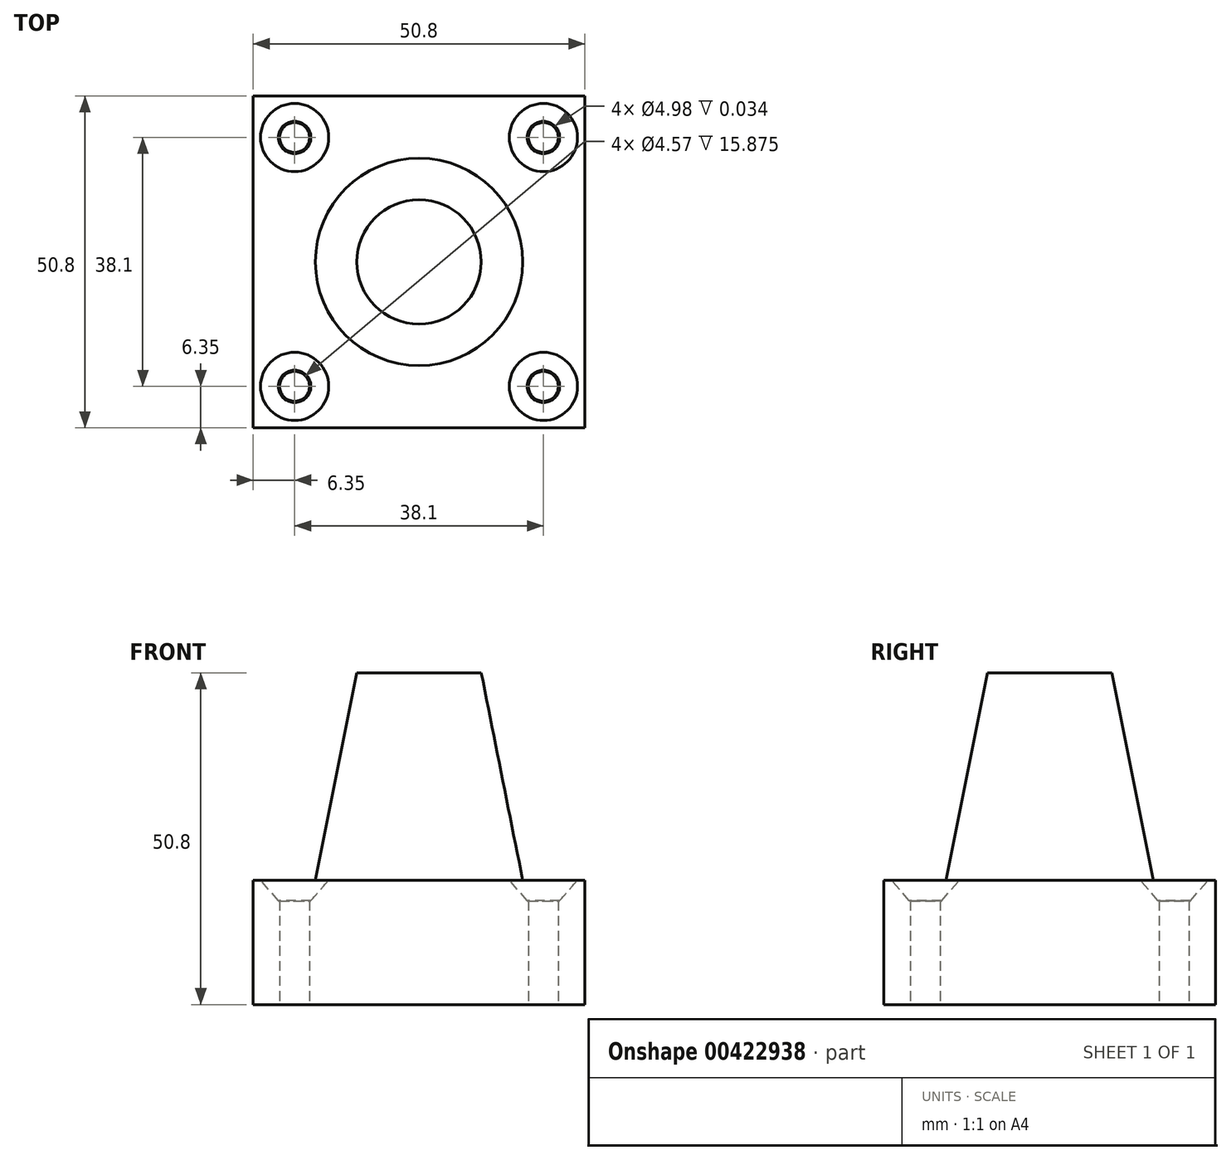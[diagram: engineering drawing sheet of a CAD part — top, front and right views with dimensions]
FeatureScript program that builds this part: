
annotation { "Feature Type Name" : "Feature", "Feature Type Description" : "" }
export const myFeature = defineFeature(function(context is Context, id is Id, definition is map)
    precondition{}
    {
        {
            var Q0;
            Q0=qCreatedBy(makeId("Top.planeOp"),FACE);
            var sketch = newSketch(context, id + "F0", { "sketchPlane" : qUnion([Q0])});
            skLineSegment(sketch, "E0.bottom", {"start": v(25.4, 25.4) * mm, "end": v(-25.4, 25.4) * mm});
            skLineSegment(sketch, "E0.top", {"start": v(25.4, -25.4) * mm, "end": v(-25.4, -25.4) * mm});
            skLineSegment(sketch, "E0.left", {"start": v(25.4, 25.4) * mm, "end": v(25.4, -25.4) * mm});
            skLineSegment(sketch, "E0.right", {"start": v(-25.4, 25.4) * mm, "end": v(-25.4, -25.4) * mm});
            skPoint(sketch, "E0.middle", {"position": v(0, 0) * mm});
            skSolve(sketch);
        }
        {
            var Q0;
            Q0=makeQuery(id+"F0.imprint","IMPRINT",FACE,{"disambiguationData":[TD([[makeQuery(id+"F0.imprint","IMPRINT",EDGE,{"derivedFrom":sQuery(id+"F0.wireOp",EDGE,"E0.bottom")}),1.0]])]});
            extrude(context, id + "F1", {"entities" : qUnion([Q0]), "depth" : 19.05 * mm});
        }
        {
            var Q0;
            Q0=makeQuery(id+"F1.opExtrude","CAP_FACE",FACE,{"disambiguationData":[OSD([sQuery(id+"F0.wireOp",EDGE,"E0.bottom"),sQuery(id+"F0.wireOp",EDGE,"E0.top"),sQuery(id+"F0.wireOp",EDGE,"E0.left"),sQuery(id+"F0.wireOp",EDGE,"E0.right")])],"isStart":false});
            cPlane(context, id + "F2", {"entities" : qUnion([Q0]), "cplaneType" : CPlaneType.OFFSET, "offset" : 31.75 * mm, "width" : 152.4 * mm, "height" : 152.4 * mm});
        }
        {
            var Q0;
            Q0=qCreatedBy(id+"F2.planeOp",FACE);
            var sketch = newSketch(context, id + "F3", { "sketchPlane" : qUnion([Q0])});
            skCircle(sketch, "E1", {"center": v(0, 0) * mm, "radius": 9.53 * mm});
            skSolve(sketch);
        }
        {
            var Q0;
            Q0=makeQuery(id+"F1.opExtrude","CAP_FACE",FACE,{"disambiguationData":[OSD([sQuery(id+"F0.wireOp",EDGE,"E0.bottom"),sQuery(id+"F0.wireOp",EDGE,"E0.top"),sQuery(id+"F0.wireOp",EDGE,"E0.left"),sQuery(id+"F0.wireOp",EDGE,"E0.right")])],"isStart":false});
            var sketch = newSketch(context, id + "F4", { "sketchPlane" : qUnion([Q0])});
            skCircle(sketch, "E2", {"center": v(0, 0) * mm, "radius": 15.88 * mm});
            skSolve(sketch);
        }
        {
            var Q1;
            Q1=makeQuery(id+"F4.imprint","IMPRINT",FACE,{"disambiguationData":[TD([[makeQuery(id+"F4.imprint","IMPRINT",EDGE,{"derivedFrom":sQuery(id+"F4.wireOp",EDGE,"E2")}),1.0]])]});
            var Q2;
            Q2=makeQuery(id+"F3.imprint","IMPRINT",FACE,{"disambiguationData":[TD([[makeQuery(id+"F3.imprint","IMPRINT",EDGE,{"derivedFrom":sQuery(id+"F3.wireOp",EDGE,"E1")}),1.0]])]});
            loft(context, id + "F5", {"operationType" : NewBodyOperationType.ADD, "sheetProfilesArray" : [{ "sheetProfileEntities" : qUnion([Q1]) }, { "sheetProfileEntities" : qUnion([Q2]) }]});
        }
        {
            var Q0;
            Q0=makeQuery(id+"F1.opExtrude","CAP_FACE",FACE,{"disambiguationData":[OSD([sQuery(id+"F0.wireOp",EDGE,"E0.bottom"),sQuery(id+"F0.wireOp",EDGE,"E0.top"),sQuery(id+"F0.wireOp",EDGE,"E0.left"),sQuery(id+"F0.wireOp",EDGE,"E0.right")])],"isStart":false});
            var sketch = newSketch(context, id + "F6", { "sketchPlane" : qUnion([Q0])});
            skCircle(sketch, "E3", {"center": v(-19.05, 19.05) * mm, "radius": 3.18 * mm});
            skCircle(sketch, "E4.1.0", {"center": v(-19.05, -19.05) * mm, "radius": 3.18 * mm});
            skCircle(sketch, "E4.2.0", {"center": v(19.05, -19.05) * mm, "radius": 3.18 * mm});
            skCircle(sketch, "E4.3.0", {"center": v(19.05, 19.05) * mm, "radius": 3.18 * mm});
            skPoint(sketch, "E4.center", {"position": v(0, 0) * mm});
            skSolve(sketch);
        }
        {
            var Q0;
            Q0=sQuery(id+"F6.wireOp",VERTEX,"E3.center");
            var Q1;
            Q1=sQuery(id+"F6.wireOp",VERTEX,"E4.3.0.center");
            var Q2;
            Q2=sQuery(id+"F6.wireOp",VERTEX,"E4.2.0.center");
            var Q3;
            Q3=sQuery(id+"F6.wireOp",VERTEX,"E4.1.0.center");
            var Q4;
            Q4=makeQuery(id+"F1.opExtrude","SWEPT_BODY",BODY,{"disambiguationData":[OSD([sQuery(id+"F0.wireOp",EDGE,"E0.bottom"),sQuery(id+"F0.wireOp",EDGE,"E0.top"),sQuery(id+"F0.wireOp",EDGE,"E0.left"),sQuery(id+"F0.wireOp",EDGE,"E0.right")])]});
            hole(context, id + "F7", {"style" : HoleStyle.C_SINK, "endStyle" : HoleEndStyle.THROUGH, "standardTappedOrClearance" : lookupTablePath({ "standard" : "ANSI", "fit" : "Close", "size" : "#10", "type" : "Clearance" }), "standardBlindInLast" : lookupTablePath({ "fit" : "Close", "standard" : "ANSI", "size" : "#10", "type" : "Clearance" }), "holeDiameter" : 4.98 * mm, "cSinkDiameter" : 10.44 * mm, "cSinkAngle" : 82 * degree, "isTappedThrough" : true, "tappedDepth" : 12.7 * mm, "tapClearance" : 3, "locations" : qUnion([Q0, Q1, Q2, Q3]), "scope" : qUnion([Q4])});
        }
        {
            var Q0;
            Q0=makeQuery(id+"F1.opExtrude","CAP_FACE",FACE,{"disambiguationData":[OSD([sQuery(id+"F0.wireOp",EDGE,"E0.bottom"),sQuery(id+"F0.wireOp",EDGE,"E0.top"),sQuery(id+"F0.wireOp",EDGE,"E0.left"),sQuery(id+"F0.wireOp",EDGE,"E0.right")])],"isStart":true});
            var sketch = newSketch(context, id + "F8", { "sketchPlane" : qUnion([Q0])});
            skCircle(sketch, "E5", {"center": v(19.05, -19.05) * mm, "radius": 2.29 * mm});
            skCircle(sketch, "E6", {"center": v(19.05, -19.05) * mm, "radius": 2.8 * mm});
            skCircle(sketch, "E7.1.0", {"center": v(19.05, 19.05) * mm, "radius": 2.8 * mm});
            skCircle(sketch, "E7.1.1", {"center": v(19.05, 19.05) * mm, "radius": 2.29 * mm});
            skCircle(sketch, "E7.2.0", {"center": v(-19.05, 19.05) * mm, "radius": 2.8 * mm});
            skCircle(sketch, "E7.2.1", {"center": v(-19.05, 19.05) * mm, "radius": 2.29 * mm});
            skCircle(sketch, "E7.3.0", {"center": v(-19.05, -19.05) * mm, "radius": 2.8 * mm});
            skCircle(sketch, "E7.3.1", {"center": v(-19.05, -19.05) * mm, "radius": 2.29 * mm});
            skPoint(sketch, "E7.center", {"position": v(0, 0) * mm});
            skSolve(sketch);
        }
        {
            var Q0;
            Q0 = qSketchRegion(id + "F8", true);
            extrude(context, id + "F9", {"entities" : qUnion([Q0]), "operationType" : NewBodyOperationType.ADD, "oppositeDirection" : true, "depth" : 15.88 * mm});
        }
    });
